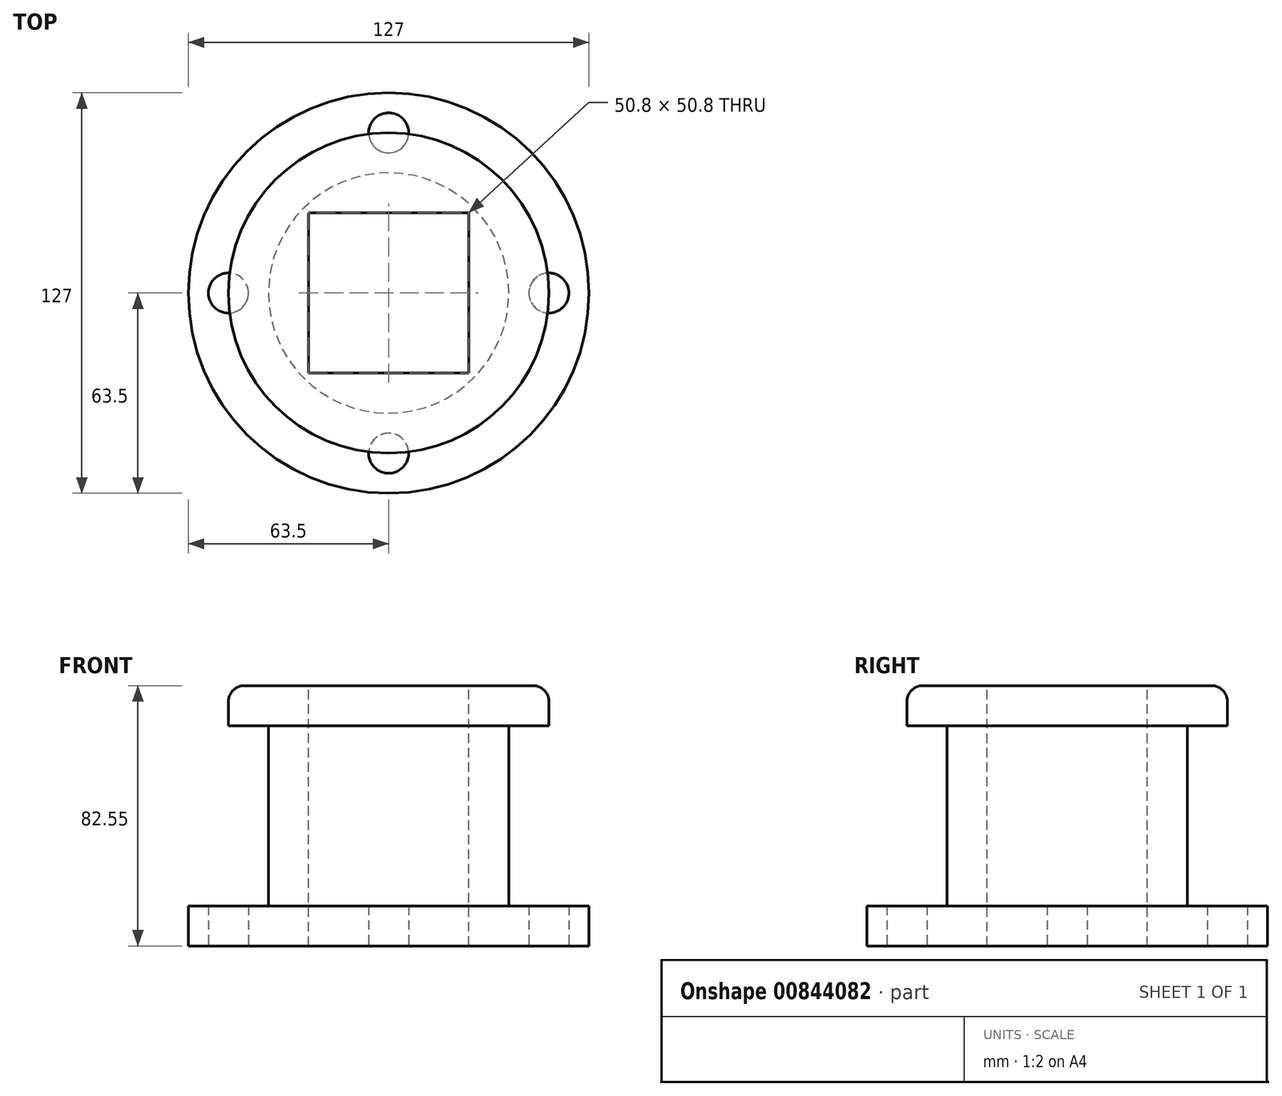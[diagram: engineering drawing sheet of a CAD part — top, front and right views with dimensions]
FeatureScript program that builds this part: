
annotation { "Feature Type Name" : "Feature", "Feature Type Description" : "" }
export const myFeature = defineFeature(function(context is Context, id is Id, definition is map)
    precondition{}
    {
        {
            var Q0;
            Q0=qCreatedBy(makeId("Top.planeOp"),FACE);
            var sketch = newSketch(context, id + "F0", { "sketchPlane" : qUnion([Q0])});
            skCircle(sketch, "E0", {"center": v(0, 0) * mm, "radius": 63.5 * mm});
            skCircle(sketch, "E1", {"center": v(0, 50.8) * mm, "radius": 6.35 * mm});
            skCircle(sketch, "E2.1.0", {"center": v(-50.8, 0) * mm, "radius": 6.35 * mm});
            skCircle(sketch, "E2.2.0", {"center": v(0, -50.8) * mm, "radius": 6.35 * mm});
            skCircle(sketch, "E2.3.0", {"center": v(50.8, 0) * mm, "radius": 6.35 * mm});
            skSolve(sketch);
        }
        {
            var Q0;
            Q0 = qSketchRegion(id + "F0", true);
            extrude(context, id + "F1", {"entities" : qUnion([Q0]), "depth" : 12.7 * mm, "offsetDistance" : 25.4 * mm});
        }
        {
            var Q0;
            Q0=makeQuery(id+"F1.opExtrude","CAP_FACE",FACE,{"disambiguationData":[OSD([sQuery(id+"F0.wireOp",EDGE,"E0"),sQuery(id+"F0.wireOp",EDGE,"E1"),sQuery(id+"F0.wireOp",EDGE,"E2.1.0"),sQuery(id+"F0.wireOp",EDGE,"E2.2.0"),sQuery(id+"F0.wireOp",EDGE,"E2.3.0"),sQuery(id+"F0.wireOp",EDGE,"UhvEWwpv-gxKA-2QbT-PQos-OZDFAWYViBGt")])],"isStart":false});
            var sketch = newSketch(context, id + "F2", { "sketchPlane" : qUnion([Q0])});
            skSolve(sketch);
        }
        {
            var Q0;
            Q0=makeQuery(id+"F2.imprint","IMPRINT",FACE,{"disambiguationData":[TD([[makeQuery(id+"F2.imprint","IMPRINT",EDGE,{"derivedFrom":makeQuery(id+"F1.opExtrude","CAP_EDGE",EDGE,{"disambiguationData":[OSD([sQuery(id+"F0.wireOp",EDGE,"E0")])],"isStart":false})}),1.0]])]});
            var sketch = newSketch(context, id + "F3", { "sketchPlane" : qUnion([Q0])});
            skCircle(sketch, "E3", {"center": v(0, 0) * mm, "radius": 38.1 * mm});
            skSolve(sketch);
        }
        {
            var Q0;
            Q0 = qSketchRegion(id + "F3", true);
            extrude(context, id + "F4", {"entities" : qUnion([Q0]), "operationType" : NewBodyOperationType.ADD, "depth" : 57.15 * mm, "offsetDistance" : 25.4 * mm});
        }
        {
            var Q0;
            Q0=makeQuery(id+"F4.opExtrude","CAP_FACE",FACE,{"disambiguationData":[OSD([sQuery(id+"F3.wireOp",EDGE,"E3")])],"isStart":false});
            var sketch = newSketch(context, id + "F5", { "sketchPlane" : qUnion([Q0])});
            skCircle(sketch, "E4", {"center": v(0, 0) * mm, "radius": 50.8 * mm});
            skSolve(sketch);
        }
        {
            var Q0;
            Q0 = qSketchRegion(id + "F5", true);
            extrude(context, id + "F6", {"entities" : qUnion([Q0]), "operationType" : NewBodyOperationType.ADD, "depth" : 12.7 * mm, "offsetDistance" : 25.4 * mm});
        }
        {
            var Q0;
            Q0=makeQuery(id+"F6.opExtrude","CAP_EDGE",EDGE,{"disambiguationData":[OSD([sQuery(id+"F5.wireOp",EDGE,"E4")])],"isStart":false});
            fillet(context, id + "F7", {"entities" : qUnion([Q0]), "radius" : 5.08 * mm, "tangentPropagation" : true, "allowEdgeOverflow" : false});
        }
        {
            var Q0;
            Q0=makeQuery(id+"F6.opExtrude","CAP_FACE",FACE,{"disambiguationData":[OSD([sQuery(id+"F5.wireOp",EDGE,"E4")])],"isStart":false});
            var sketch = newSketch(context, id + "F8", { "sketchPlane" : qUnion([Q0])});
            skLineSegment(sketch, "E5.bottom", {"start": v(-25.4, 25.4) * mm, "end": v(25.4, 25.4) * mm});
            skLineSegment(sketch, "E5.top", {"start": v(-25.4, -25.4) * mm, "end": v(25.4, -25.4) * mm});
            skLineSegment(sketch, "E5.left", {"start": v(-25.4, 25.4) * mm, "end": v(-25.4, -25.4) * mm});
            skLineSegment(sketch, "E5.right", {"start": v(25.4, 25.4) * mm, "end": v(25.4, -25.4) * mm});
            skPoint(sketch, "E6.end.orphan", {"position": v(0, 25.4) * mm});
            skPoint(sketch, "E6.start.orphan", {"position": v(0, 0) * mm});
            skSolve(sketch);
        }
        {
            var Q0;
            Q0 = qSketchRegion(id + "F8", true);
            extrude(context, id + "F9", {"entities" : qUnion([Q0]), "operationType" : NewBodyOperationType.REMOVE, "oppositeDirection" : true, "depth" : 101.6 * mm, "offsetDistance" : 25.4 * mm});
        }
    });
